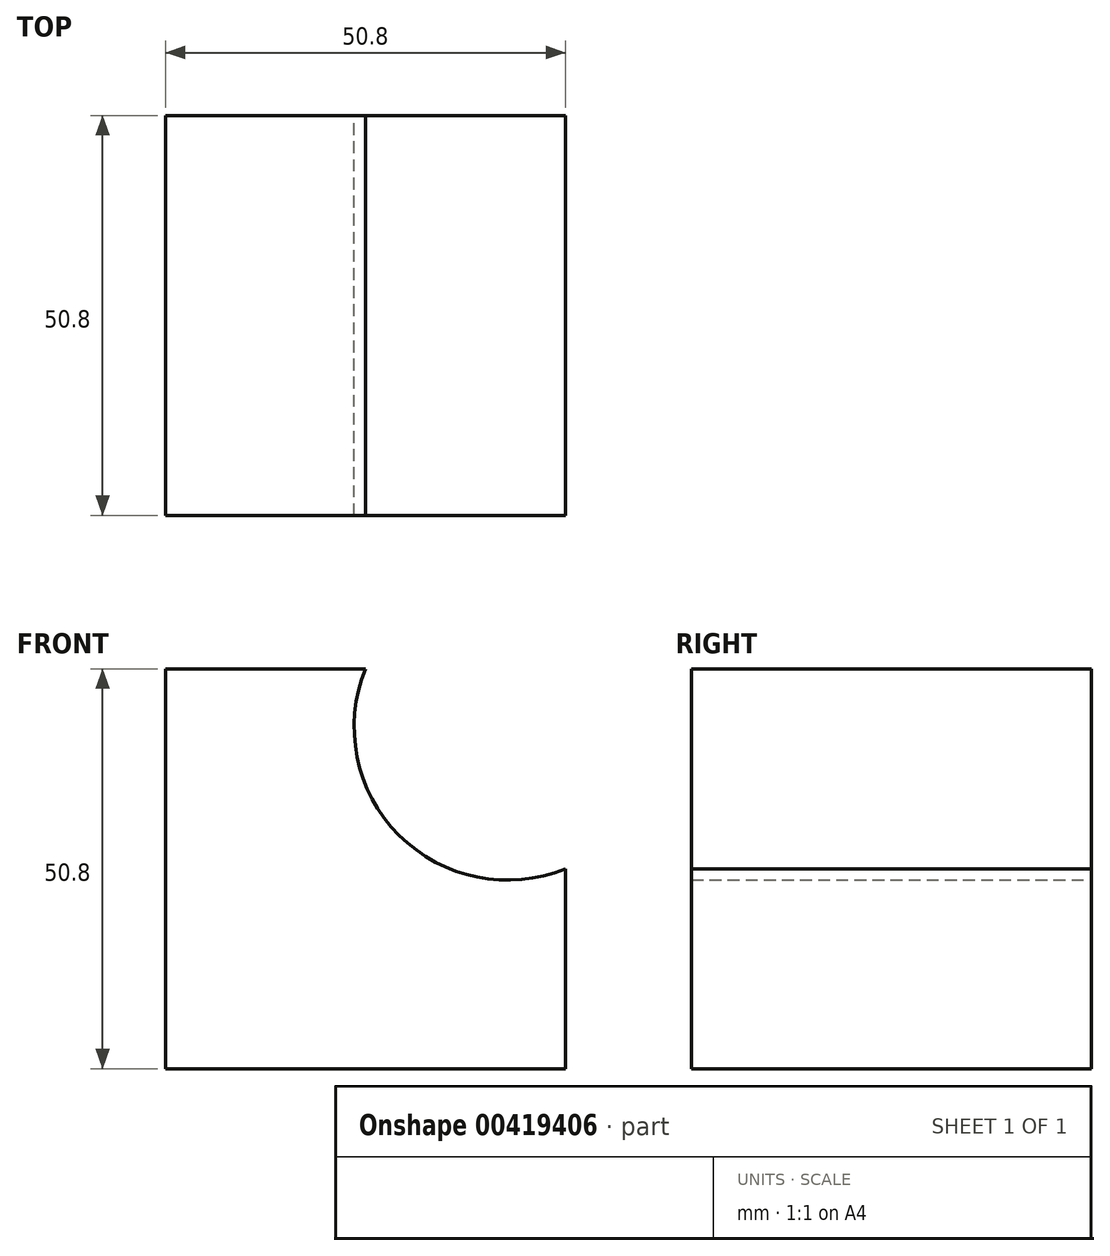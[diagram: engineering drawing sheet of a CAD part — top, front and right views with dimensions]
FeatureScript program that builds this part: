
annotation { "Feature Type Name" : "Feature", "Feature Type Description" : "" }
export const myFeature = defineFeature(function(context is Context, id is Id, definition is map)
    precondition{}
    {
        {
            var Q0;
            Q0=qCreatedBy(makeId("Front.planeOp"),FACE);
            var sketch = newSketch(context, id + "F0", { "sketchPlane" : qUnion([Q0])});
            skLineSegment(sketch, "E0", {"start": v(0, 0) * mm, "end": v(-50.8, 0) * mm});
            skLineSegment(sketch, "E1", {"start": v(-50.8, 0) * mm, "end": v(-50.8, 50.8) * mm});
            skLineSegment(sketch, "E2", {"start": v(-50.8, 50.8) * mm, "end": v(-25.4, 50.8) * mm});
            skLineSegment(sketch, "E3", {"start": v(0, 0) * mm, "end": v(0, 25.4) * mm});
            skArc(sketch, "E4", {"start": v(-25.4, 50.8) * mm, "mid": v(-21.15, 29.65) * mm, "end": v(0, 25.4) * mm});
            skSolve(sketch);
        }
        {
            var Q0;
            Q0 = qSketchRegion(id + "F0", true);
            extrude(context, id + "F1", {"entities" : qUnion([Q0]), "depth" : 50.8 * mm});
        }
    });
